# Revit family: Zócalo (Z100-Z500). C-1
name_source: partatom
category: Modelos genéricos
units: mm (PartAtom-declared; Revit-internal decimal feet)

## family parameters
Compartido = No
Corte con vacíos al cargar = No
Cota de conector redondo = Diámetro de uso
Puede alojar armadura = No
Punto de cálculo de habitación = No
Se basa en plano de trabajo = No
Siempre vertical = No
Tipo de pieza = Normal

## types (4) — shared parameters
Descripción = Pieza de hormigón polímero con anclaje de acero inoxidable.
Fabricante = ULMA Architectural Solutions
Material = Hormigón polímero STONEO. Color C-1
URL = https://www.ulmaarchitectural.com
zero-valued in all types: Elevación por defecto

## per-type parameters (varying)
| type | Altura | Altura anclaje | Altura anclaje 2 | Ancho zócalo | Modelo | Radio | Visibilidad anclajes |
| Z100 | 100 mm  [stored 0.328084 ft] | 50 mm  [stored 0.164042 ft] | 150 mm | 20 mm | Zócalo Z100 | 30 mm | No |
| Z175 | 175 mm  [stored 0.574147 ft] | 88 mm | 263 mm | 22 mm  [stored 0.0721785 ft] | Zócalo Z175 | 30 mm | No |
| Z325 | 325 mm  [stored 1.06627 ft] | 163 mm | 488 mm | 25 mm  [stored 0.082021 ft] | Zócalo Z325 | 40 mm  [stored 0.131234 ft] | No |
| Z500 | 500 mm  [stored 1.64042 ft] | 125 mm  [stored 0.410105 ft] | 375 mm  [stored 1.23031 ft] | 25 mm  [stored 0.082021 ft] | Zócalo Z500 | 40 mm  [stored 0.131234 ft] | Sí |

note: column(s) folded — value = type name in every type: Código de montaje

note: [stored X ft] marks values corroborated as IEEE doubles in the binary element streams (Revit-internal decimal feet)
